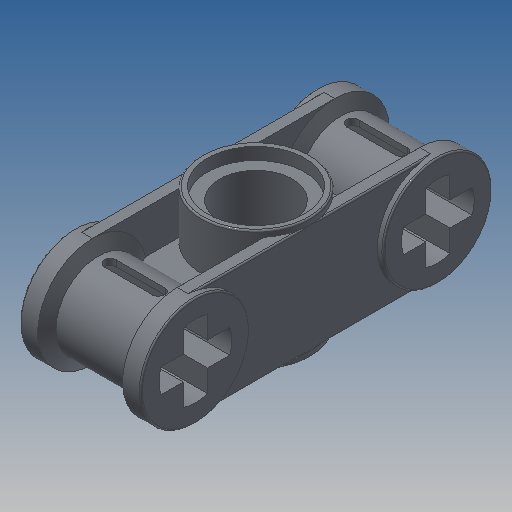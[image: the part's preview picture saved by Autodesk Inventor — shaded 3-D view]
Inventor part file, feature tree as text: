
AUTODESK INVENTOR PART (.ipt)
format: ipt  version: 2022.2 (Build 262287000, 287)  size: 393,216 bytes
history: native  units: in
note: dims shown in document units (in); Inventor stores cm internally (conversion verified against a paired STEP export)
features: extrude x6, sketch x4, mirror x2, plane x1, revolve x1, fillet x1
ambient origin geometry x8: Origin, YZ Plane, XZ Plane, XY Plane, X Axis, Y Axis, Z Axis, Center Point
bodies: Solid1 (feature_tree)
feature tree (15):
  sketch  "Sketch2"  dims[d0=0.2835in d1=0.189in]
  extrude  "Extrusion1"  Depth=0.189in
  plane  "Work Plane1"
  extrude  "Extrusion2"  Depth=0.315in TaperAngle=0.0deg
  extrude  "Extrusion4"  Depth=0.2835in
  extrude  "Extrusion3"  Depth=0.0039in TaperAngle=0.0deg
  mirror  "Mirror1"
  revolve  "Revolution1"  [1 undecoded]
  extrude  "Extrusion5"  Depth=0.0039in TaperAngle=0.0deg
  extrude  "Extrusion6"  Depth=0.0039in
  mirror  "Mirror2"
  fillet  "Fillet1"  Radius=0.0472in
  sketch  "Sketch3"  dims[d2=0.315in d3=0.315in d4=0.0in]
  sketch  "Sketch4"  dims[d5=0.0in d6=0.2835in]
  sketch  "Sketch5"  dims[d7=0.0315in d8=0.4724in d9=0.0in d10=0.252in d11=0.0315in d12=0.0in d13=0.2835in d14=0.0472in d15=0.315in d16=0.2205in d17=0.063in d18=0.0315in d19=0.1575in d20=90.0deg d21=0.063in d22=0.0in d23=0.063in d24=0.0in d25=0.189in d26=0.063in d27=0.063in d28=0.0in d29=0.0039in]
note: 1 required parameter value undecoded (feature->parameter linkage not recoverable at this tier; creation-order binding heuristic only, values carry confidence <= 0.55)
